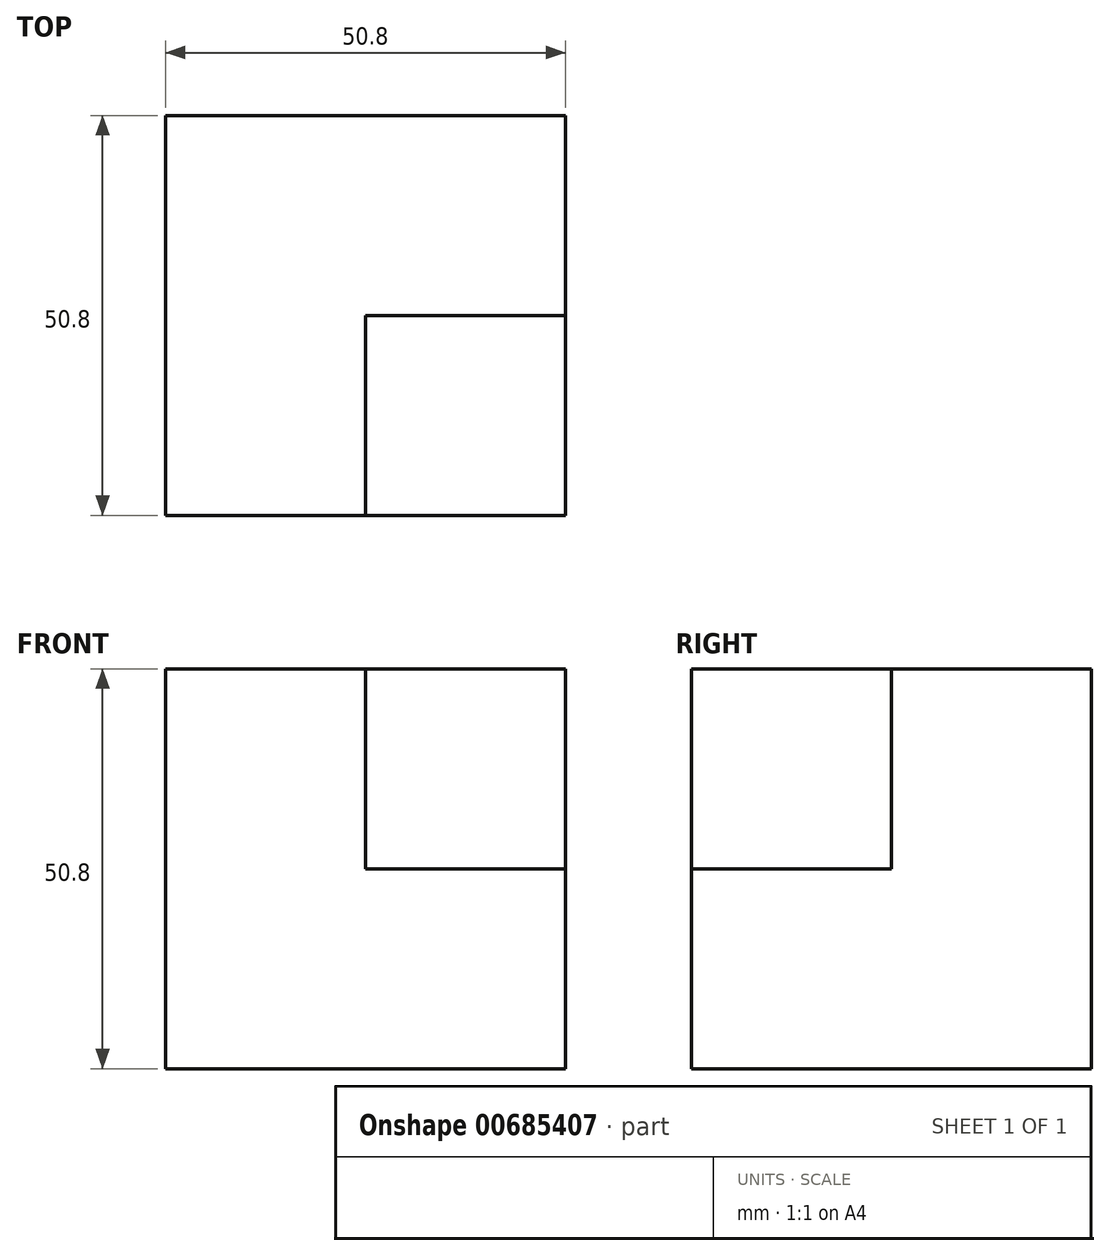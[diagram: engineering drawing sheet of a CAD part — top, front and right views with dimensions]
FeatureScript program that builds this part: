
annotation { "Feature Type Name" : "Feature", "Feature Type Description" : "" }
export const myFeature = defineFeature(function(context is Context, id is Id, definition is map)
    precondition{}
    {
        {
            var Q0;
            Q0=qCreatedBy(makeId("Front.planeOp"),FACE);
            var sketch = newSketch(context, id + "F0", { "sketchPlane" : qUnion([Q0])});
            skLineSegment(sketch, "E0", {"start": v(0, 0) * mm, "end": v(-50.8, 0) * mm});
            skLineSegment(sketch, "E1", {"start": v(-50.8, 0) * mm, "end": v(-50.8, 50.8) * mm});
            skLineSegment(sketch, "E2", {"start": v(-50.8, 50.8) * mm, "end": v(0, 50.8) * mm});
            skLineSegment(sketch, "E3", {"start": v(0, 50.8) * mm, "end": v(0, 0) * mm});
            skSolve(sketch);
        }
        {
            var Q0;
            Q0=makeQuery(id+"F0.imprint","IMPRINT",FACE,{"disambiguationData":[TD([[makeQuery(id+"F0.imprint","IMPRINT",EDGE,{"derivedFrom":sQuery(id+"F0.wireOp",EDGE,"E0")}),-1.0]])]});
            extrude(context, id + "F1", {"entities" : qUnion([Q0]), "depth" : 50.8 * mm, "offsetDistance" : 25.4 * mm});
        }
        {
            var Q0;
            Q0=makeQuery(id+"F1.opExtrude","CAP_FACE",FACE,{"disambiguationData":[OSD([sQuery(id+"F0.wireOp",EDGE,"E0"),sQuery(id+"F0.wireOp",EDGE,"E1"),sQuery(id+"F0.wireOp",EDGE,"E2"),sQuery(id+"F0.wireOp",EDGE,"E3")])],"isStart":false});
            var sketch = newSketch(context, id + "F2", { "sketchPlane" : qUnion([Q0])});
            skLineSegment(sketch, "E4.bottom", {"start": v(-25.4, 50.8) * mm, "end": v(0, 50.8) * mm});
            skLineSegment(sketch, "E4.top", {"start": v(-25.4, 25.4) * mm, "end": v(0, 25.4) * mm});
            skLineSegment(sketch, "E4.left", {"start": v(-25.4, 50.8) * mm, "end": v(-25.4, 25.4) * mm});
            skLineSegment(sketch, "E4.right", {"start": v(0, 50.8) * mm, "end": v(0, 25.4) * mm});
            skSolve(sketch);
        }
        {
            var Q0;
            Q0 = qSketchRegion(id + "F2", true);
            extrude(context, id + "F3", {"entities" : qUnion([Q0]), "operationType" : NewBodyOperationType.REMOVE, "oppositeDirection" : true, "depth" : 25.4 * mm, "offsetDistance" : 25.4 * mm});
        }
    });
